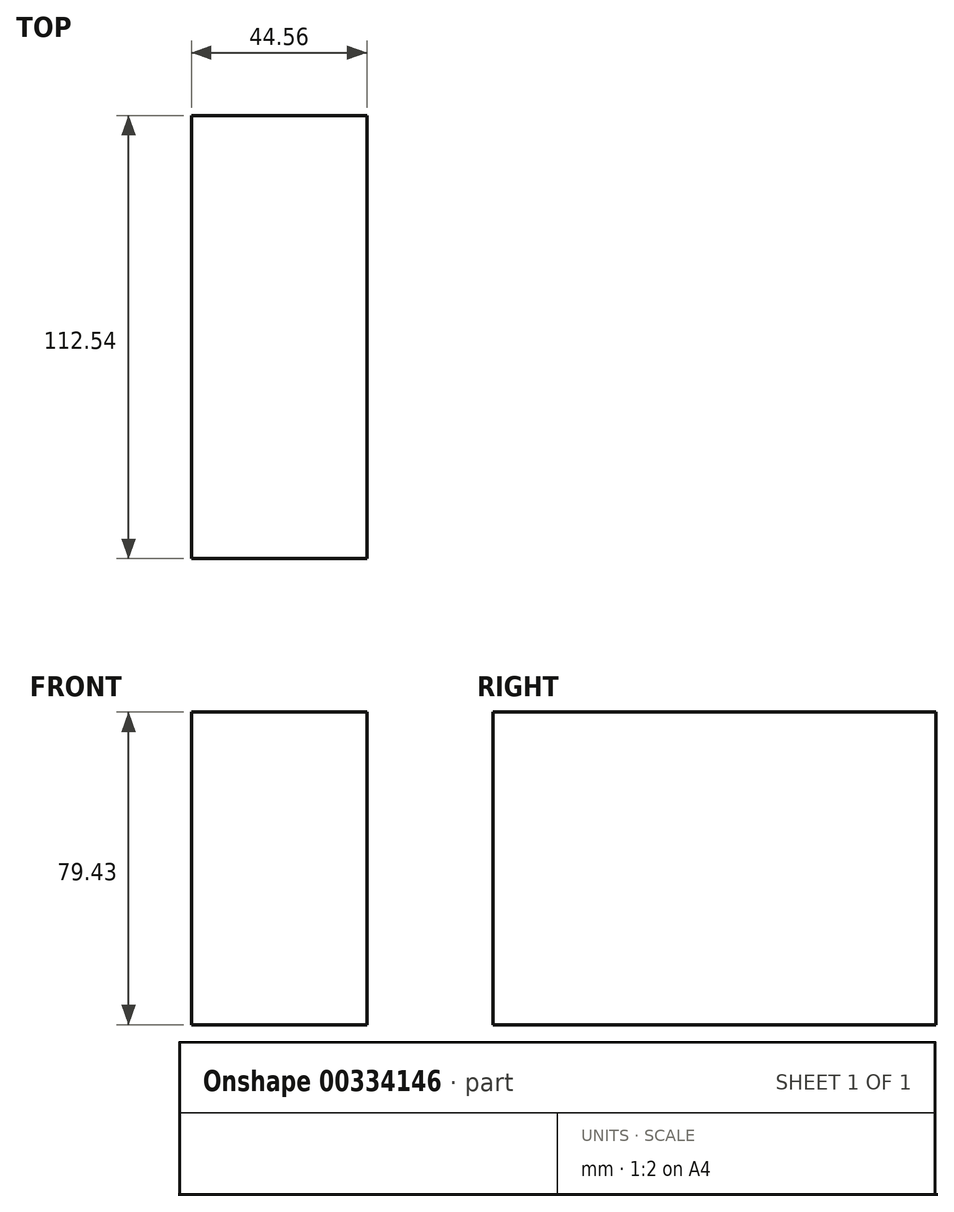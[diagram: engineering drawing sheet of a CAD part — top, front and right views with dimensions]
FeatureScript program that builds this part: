
annotation { "Feature Type Name" : "Feature", "Feature Type Description" : "" }
export const myFeature = defineFeature(function(context is Context, id is Id, definition is map)
    precondition{}
    {
        {
            var Q0;
            Q0=qCreatedBy(makeId("Front.planeOp"),FACE);
            var sketch = newSketch(context, id + "F0", { "sketchPlane" : qUnion([Q0])});
            skLineSegment(sketch, "E0.bottom", {"start": v(44.56, 39.27) * mm, "end": v(0, 39.27) * mm});
            skLineSegment(sketch, "E0.top", {"start": v(44.56, -40.16) * mm, "end": v(0, -40.16) * mm});
            skLineSegment(sketch, "E0.left", {"start": v(44.56, 39.27) * mm, "end": v(44.56, -40.16) * mm});
            skLineSegment(sketch, "E0.right", {"start": v(0, 39.27) * mm, "end": v(0, -40.16) * mm});
            skSolve(sketch);
        }
        {
            var Q0;
            Q0=makeQuery(id+"F0.imprint","IMPRINT",FACE,{"disambiguationData":[TD([[makeQuery(id+"F0.imprint","IMPRINT",EDGE,{"derivedFrom":sQuery(id+"F0.wireOp",EDGE,"E0.bottom")}),1.0]])]});
            extrude(context, id + "F1", {"entities" : qUnion([Q0]), "depth" : 112.54 * mm});
        }
    });
